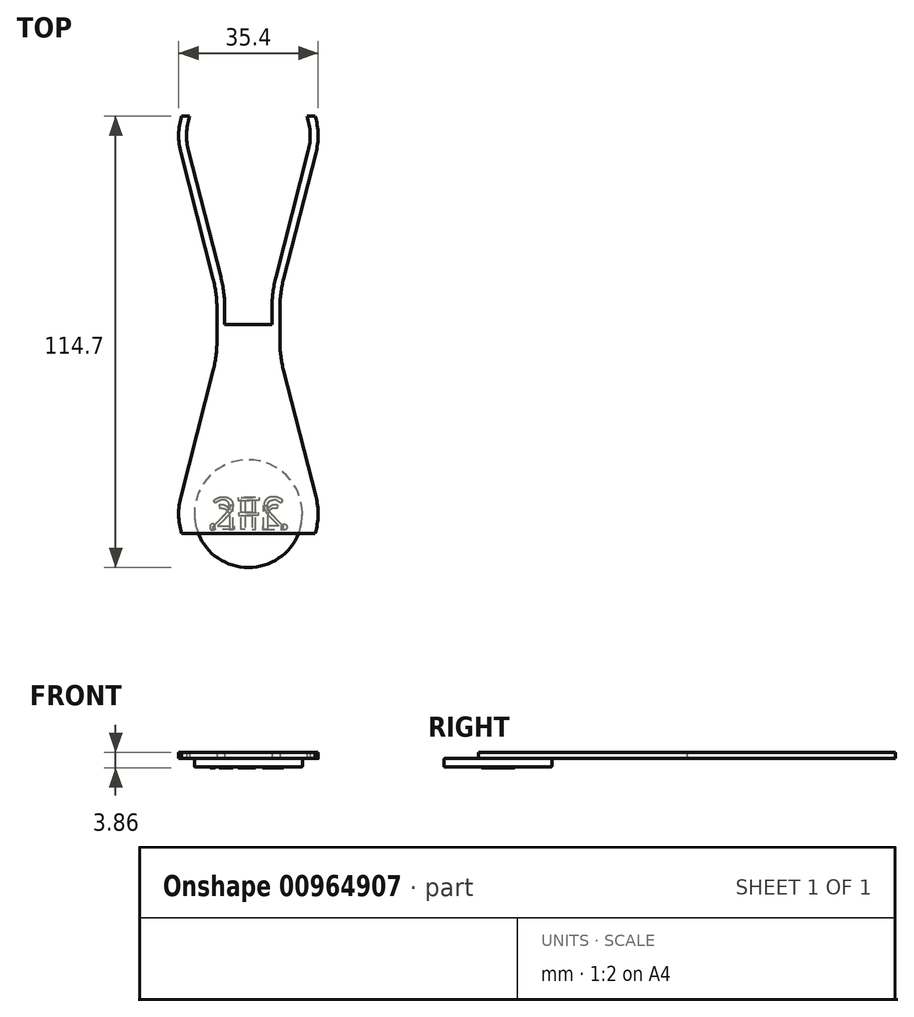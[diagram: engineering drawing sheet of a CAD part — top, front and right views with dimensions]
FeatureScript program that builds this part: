
annotation { "Feature Type Name" : "Feature", "Feature Type Description" : "" }
export const myFeature = defineFeature(function(context is Context, id is Id, definition is map)
    precondition{}
    {
        {
            var Q0;
            Q0=qCreatedBy(makeId("Top.planeOp"),FACE);
            var sketch = newSketch(context, id + "F0", { "sketchPlane" : qUnion([Q0])});
            skCircle(sketch, "E0", {"center": v(0, 0) * mm, "radius": 13.7 * mm});
            skSolve(sketch);
        }
        {
            var Q0;
            Q0 = qSketchRegion(id + "F0", true);
            extrude(context, id + "F1", {"entities" : qUnion([Q0]), "depth" : 1.07 * mm, "offsetDistance" : 25 * mm});
        }
        {
            var Q0;
            Q0=makeQuery(id+"F1.opExtrude","CAP_EDGE",EDGE,{"disambiguationData":[OSD([sQuery(id+"F0.wireOp",EDGE,"E0")])],"isStart":false});
            fillet(context, id + "F2", {"entities" : qUnion([Q0]), "radius" : 0.2 * mm, "tangentPropagation" : true, "allowEdgeOverflow" : false});
        }
        {
            var Q0;
            Q0=makeQuery(id+"F1.opExtrude","CAP_FACE",FACE,{"disambiguationData":[OSD([sQuery(id+"F0.wireOp",EDGE,"E0")])],"isStart":false});
            var sketch = newSketch(context, id + "F3", { "sketchPlane" : qUnion([Q0])});
            skText(sketch, "E1", { "text": "2Fr.", "fontName": "OpenSans-Regular.ttf"});
            const initialGuessF3  = {"E1": [-0.0095, -0.004, 1, 0, 0.00822]};
            skSetInitialGuess(sketch, initialGuessF3);
            skSolve(sketch);
        }
        {
            var Q0;
            Q0 = qSketchRegion(id + "F3", true);
            extrude(context, id + "F4", {"entities" : qUnion([Q0]), "operationType" : NewBodyOperationType.ADD, "depth" : 0.2 * mm, "offsetDistance" : 25 * mm});
        }
        {
            var Q0;
            Q0=makeQuery(id+"F1.opExtrude","CAP_FACE",FACE,{"disambiguationData":[OSD([sQuery(id+"F0.wireOp",EDGE,"E0")])],"isStart":true});
            var sketch = newSketch(context, id + "F5", { "sketchPlane" : qUnion([Q0])});
            skLineSegment(sketch, "E2", {"start": v(0, -13.7) * mm, "end": v(0, 13.7) * mm, "construction": true});
            skSolve(sketch);
        }
        {
            var Q0;
            Q0=makeQuery(id+"F1.opExtrude","SWEPT_BODY",BODY,{"disambiguationData":[OSD([sQuery(id+"F0.wireOp",EDGE,"E0")])]});
            var Q1;
            Q1=sQuery(id+"F5.wireOp",EDGE,"E2");
            circularPattern(context, id + "F6", {"operationType" : NewBodyOperationType.ADD, "entities" : qUnion([Q0]), "axis" : qUnion([Q1]), "angle" : 180 * degree, "instanceCount" : 2});
        }
        {
            var Q0;
            Q0=qCreatedBy(makeId("Top.planeOp"),FACE);
            var sketch = newSketch(context, id + "F7", { "sketchPlane" : qUnion([Q0])});
            skArc(sketch, "E3.0", {"start": v(14.88, -5) * mm, "mid": v(15.69, -0.57) * mm, "end": v(15.2, 3.9) * mm});
            skArc(sketch, "E4.0", {"start": v(-17.14, 4.4) * mm, "mid": v(-17.7, -0.3) * mm, "end": v(-16.98, -5) * mm});
            skLineSegment(sketch, "E5", {"start": v(8, 48) * mm, "end": v(8, 43.8) * mm});
            skLineSegment(sketch, "E6", {"start": v(8.94, 36.33) * mm, "end": v(17.14, 4.4) * mm});
            skLineSegment(sketch, "E7", {"start": v(8, 48) * mm, "end": v(0, 48) * mm});
            skPoint(sketch, "E8.visualSharp", {"position": v(8, 40) * mm});
            skArc(sketch, "E8.filletArc", {"start": v(8, 43.8) * mm, "mid": v(8.24, 40.03) * mm, "end": v(8.94, 36.33) * mm});
            skLineSegment(sketch, "E9.MirrorCS", {"start": v(-8, 48) * mm, "end": v(0, 48) * mm});
            skLineSegment(sketch, "E10.MirrorCS", {"start": v(-8, 48) * mm, "end": v(-8, 43.8) * mm});
            skArc(sketch, "E11.MirrorCS", {"start": v(-8, 43.8) * mm, "mid": v(-8.24, 40.03) * mm, "end": v(-8.94, 36.33) * mm});
            skLineSegment(sketch, "E12.MirrorCS", {"start": v(-8.94, 36.33) * mm, "end": v(-17.14, 4.4) * mm});
            skLineSegment(sketch, "E13", {"start": v(-16.98, -5) * mm, "end": v(16.98, -5) * mm});
            skArc(sketch, "E14.trimOffspring", {"start": v(16.98, -5) * mm, "mid": v(17.7, -0.3) * mm, "end": v(17.14, 4.4) * mm});
            skLineSegment(sketch, "E15.0", {"start": v(7, 35.83) * mm, "end": v(15.2, 3.9) * mm});
            skArc(sketch, "E15.1", {"start": v(6, 43.8) * mm, "mid": v(6.25, 39.78) * mm, "end": v(7, 35.83) * mm});
            skLineSegment(sketch, "E15.2", {"start": v(6, 48) * mm, "end": v(6, 43.8) * mm});
            skLineSegment(sketch, "E16.MirrorCS", {"start": v(-6, 48) * mm, "end": v(-6, 43.8) * mm});
            skArc(sketch, "E17.MirrorCS", {"start": v(-6, 43.8) * mm, "mid": v(-6.25, 39.78) * mm, "end": v(-7, 35.83) * mm});
            skLineSegment(sketch, "E18.MirrorCS", {"start": v(-7, 35.83) * mm, "end": v(-15.2, 3.9) * mm});
            skArc(sketch, "E19.trimOffspring", {"start": v(-15.2, 3.9) * mm, "mid": v(-15.69, -0.57) * mm, "end": v(-14.88, -5) * mm});
            skLineSegment(sketch, "E20.left", {"start": v(-3, 30) * mm, "end": v(-3, 20) * mm});
            skLineSegment(sketch, "E21.MirrorCS", {"start": v(3, 30) * mm, "end": v(3, 20) * mm});
            skLineSegment(sketch, "E22.MirrorCS", {"start": v(8, 48) * mm, "end": v(8, 52.2) * mm});
            skArc(sketch, "E23.MirrorCS", {"start": v(8, 52.2) * mm, "mid": v(8.24, 55.97) * mm, "end": v(8.94, 59.67) * mm});
            skLineSegment(sketch, "E24.MirrorCS", {"start": v(8.94, 59.67) * mm, "end": v(17.14, 91.6) * mm});
            skArc(sketch, "E25.MirrorCS", {"start": v(16.98, 101) * mm, "mid": v(17.7, 96.3) * mm, "end": v(17.14, 91.6) * mm});
            skLineSegment(sketch, "E26.MirrorCS", {"start": v(-8, 48) * mm, "end": v(-8, 52.2) * mm});
            skArc(sketch, "E27.MirrorCS", {"start": v(-8, 52.2) * mm, "mid": v(-8.24, 55.97) * mm, "end": v(-8.94, 59.67) * mm});
            skLineSegment(sketch, "E28.MirrorCS", {"start": v(-8.94, 59.67) * mm, "end": v(-17.14, 91.6) * mm});
            skArc(sketch, "E29.MirrorCS", {"start": v(-17.14, 91.6) * mm, "mid": v(-17.7, 96.3) * mm, "end": v(-16.98, 101) * mm});
            skLineSegment(sketch, "E30.MirrorCS", {"start": v(-16.98, 101) * mm, "end": v(16.98, 101) * mm});
            skArc(sketch, "E31.MirrorCS", {"start": v(-15.2, 92.1) * mm, "mid": v(-15.69, 96.57) * mm, "end": v(-14.88, 101) * mm});
            skLineSegment(sketch, "E32.MirrorCS", {"start": v(-7, 60.17) * mm, "end": v(-15.2, 92.1) * mm});
            skLineSegment(sketch, "E33.MirrorCS", {"start": v(-6, 48) * mm, "end": v(-6, 52.2) * mm});
            skArc(sketch, "E34.MirrorCS", {"start": v(-6, 52.2) * mm, "mid": v(-6.25, 56.22) * mm, "end": v(-7, 60.17) * mm});
            skArc(sketch, "E35.MirrorCS", {"start": v(14.88, 101) * mm, "mid": v(15.69, 96.57) * mm, "end": v(15.2, 92.1) * mm});
            skLineSegment(sketch, "E36.MirrorCS", {"start": v(7, 60.17) * mm, "end": v(15.2, 92.1) * mm});
            skArc(sketch, "E37.MirrorCS", {"start": v(6, 52.2) * mm, "mid": v(6.25, 56.22) * mm, "end": v(7, 60.17) * mm});
            skLineSegment(sketch, "E38.MirrorCS", {"start": v(6, 48) * mm, "end": v(6, 52.2) * mm});
            skLineSegment(sketch, "E39.MirrorCS", {"start": v(-3, 66) * mm, "end": v(-3, 76) * mm});
            skLineSegment(sketch, "E40.MirrorCS", {"start": v(3, 66) * mm, "end": v(3, 76) * mm});
            skSolve(sketch);
        }
        {
            var Q0;
            {var subQ6=sQuery(id+"F7.wireOp",EDGE,"E31.MirrorCS");Q0=makeQuery(id+"F7.imprint","IMPRINT",FACE,{"disambiguationData":[TD([[makeQuery(id+"F7.imprint","IMPRINT",EDGE,{"derivedFrom":subQ6}),-1.0]])]});}
            var Q1;
            {var subQ0=sQuery(id+"F7.wireOp",EDGE,"E22.MirrorCS");Q1=makeQuery(id+"F7.imprint","IMPRINT",FACE,{"disambiguationData":[TD([[makeQuery(id+"F7.imprint","IMPRINT",EDGE,{"derivedFrom":subQ0}),1.0]])]});}
            var Q2;
            {var subQ0=sQuery(id+"F7.wireOp",EDGE,"E26.MirrorCS");Q2=makeQuery(id+"F7.imprint","IMPRINT",FACE,{"disambiguationData":[TD([[makeQuery(id+"F7.imprint","IMPRINT",EDGE,{"derivedFrom":subQ0}),-1.0]])]});}
            var Q3;
            {var subQ1=sQuery(id+"F7.wireOp",EDGE,"E3.0");Q3=makeQuery(id+"F7.imprint","IMPRINT",FACE,{"disambiguationData":[TD([[makeQuery(id+"F7.imprint","IMPRINT",EDGE,{"derivedFrom":subQ1}),1.0]])]});}
            var Q4;
            {var subQ3=sQuery(id+"F7.wireOp",EDGE,"E4.0");Q4=makeQuery(id+"F7.imprint","IMPRINT",FACE,{"disambiguationData":[TD([[makeQuery(id+"F7.imprint","IMPRINT",EDGE,{"derivedFrom":subQ3}),1.0]])]});}
            var Q5;
            {var subQ5=sQuery(id+"F7.wireOp",EDGE,"E3.0");Q5=makeQuery(id+"F7.imprint","IMPRINT",FACE,{"disambiguationData":[TD([[makeQuery(id+"F7.imprint","IMPRINT",EDGE,{"derivedFrom":subQ5}),-1.0]])]});}
            extrude(context, id + "F8", {"entities" : qUnion([Q0, Q1, Q2, Q3, Q4, Q5]), "depth" : 1.5 * mm, "offsetDistance" : 25 * mm});
        }
        {
            var Q0;
            Q0=makeQuery(id+"F8.opExtrude","SWEPT_BODY",BODY,{"disambiguationData":[OSD([sQuery(id+"F7.wireOp",EDGE,"E4.0"),sQuery(id+"F7.wireOp",EDGE,"E5"),sQuery(id+"F7.wireOp",EDGE,"E6"),sQuery(id+"F7.wireOp",EDGE,"E8.filletArc"),sQuery(id+"F7.wireOp",EDGE,"E10.MirrorCS"),sQuery(id+"F7.wireOp",EDGE,"E11.MirrorCS"),sQuery(id+"F7.wireOp",EDGE,"E12.MirrorCS"),sQuery(id+"F7.wireOp",EDGE,"E13"),sQuery(id+"F7.wireOp",EDGE,"E14.trimOffspring"),sQuery(id+"F7.wireOp",EDGE,"E22.MirrorCS"),sQuery(id+"F7.wireOp",EDGE,"E23.MirrorCS"),sQuery(id+"F7.wireOp",EDGE,"E24.MirrorCS"),sQuery(id+"F7.wireOp",EDGE,"E25.MirrorCS"),sQuery(id+"F7.wireOp",EDGE,"E26.MirrorCS"),sQuery(id+"F7.wireOp",EDGE,"E27.MirrorCS"),sQuery(id+"F7.wireOp",EDGE,"E28.MirrorCS"),sQuery(id+"F7.wireOp",EDGE,"E29.MirrorCS"),sQuery(id+"F7.wireOp",EDGE,"E30.MirrorCS")])]});
            var Q1;
            Q1=qCreatedBy(makeId("Top.planeOp"),FACE);
            transform(context, id + "F9", {"entities" : qUnion([Q0]), "transformType" : TransformType.TRANSLATION_DISTANCE, "transformDirection" : qUnion([Q1]), "distance" : 1.07 * mm, "makeCopy" : false});
        }
    });
